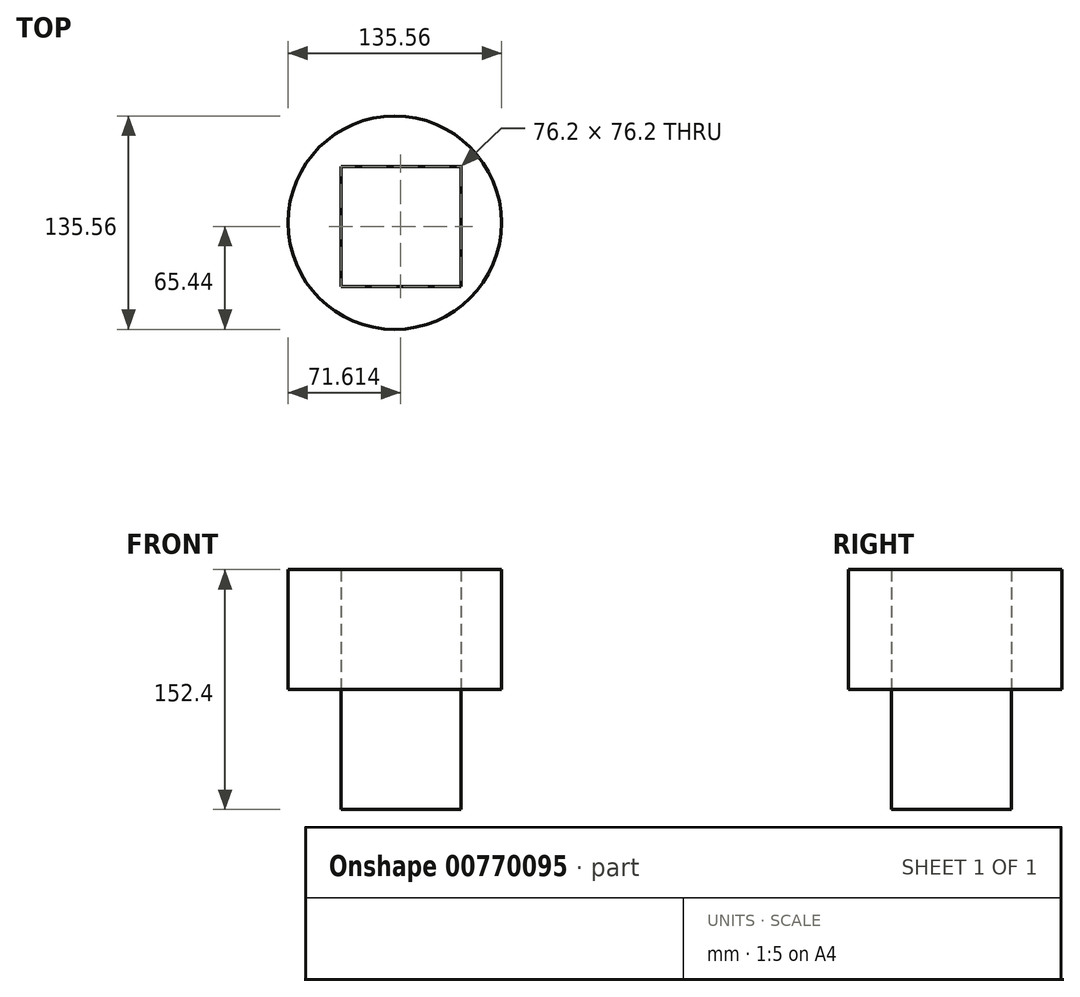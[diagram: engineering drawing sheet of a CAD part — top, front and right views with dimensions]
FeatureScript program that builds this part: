
annotation { "Feature Type Name" : "Feature", "Feature Type Description" : "" }
export const myFeature = defineFeature(function(context is Context, id is Id, definition is map)
    precondition{}
    {
        {
            var Q0;
            Q0=qCreatedBy(makeId("Front.planeOp"),FACE);
            var sketch = newSketch(context, id + "F0", { "sketchPlane" : qUnion([Q0])});
            skLineSegment(sketch, "E0.bottom", {"start": v(-28.1, 30.3) * mm, "end": v(48.1, 30.3) * mm});
            skLineSegment(sketch, "E0.top", {"start": v(-28.1, -45.9) * mm, "end": v(48.1, -45.9) * mm});
            skLineSegment(sketch, "E0.left", {"start": v(-28.1, 30.3) * mm, "end": v(-28.1, -45.9) * mm});
            skLineSegment(sketch, "E0.right", {"start": v(48.1, 30.3) * mm, "end": v(48.1, -45.9) * mm});
            skSolve(sketch);
        }
        {
            var Q0;
            Q0=makeQuery(id+"F0.imprint","IMPRINT",FACE,{"disambiguationData":[TD([[makeQuery(id+"F0.imprint","IMPRINT",EDGE,{"derivedFrom":sQuery(id+"F0.wireOp",EDGE,"E0.bottom")}),-1.0]])]});
            extrude(context, id + "F1", {"entities" : qUnion([Q0]), "depth" : 76.2 * mm, "offsetDistance" : 25.4 * mm});
        }
        {
            var Q0;
            Q0=makeQuery(id+"F1.opExtrude","SWEPT_FACE",FACE,{"disambiguationData":[OSD([sQuery(id+"F0.wireOp",EDGE,"E0.bottom")])]});
            var sketch = newSketch(context, id + "F2", { "sketchPlane" : qUnion([Q0])});
            skCircle(sketch, "E1", {"center": v(6.17, -35.76) * mm, "radius": 67.78 * mm});
            skSolve(sketch);
        }
        {
            var Q0;
            Q0=makeQuery(id+"F2.imprint","IMPRINT",FACE,{"disambiguationData":[TD([[makeQuery(id+"F2.imprint","IMPRINT",EDGE,{"derivedFrom":sQuery(id+"F2.wireOp",EDGE,"E1")}),1.0]])]});
            extrude(context, id + "F3", {"entities" : qUnion([Q0]), "depth" : 76.2 * mm, "offsetDistance" : 25.4 * mm});
        }
    });
